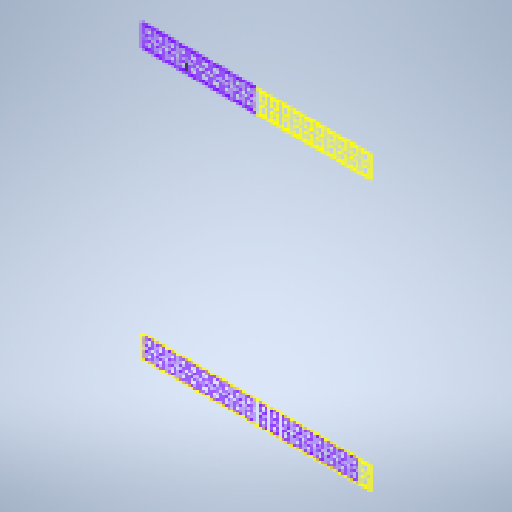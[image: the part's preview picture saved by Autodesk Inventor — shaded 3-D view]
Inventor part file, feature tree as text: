
AUTODESK INVENTOR PART (.ipt)
format: ipt  version: 2024.2 (Build 282272000, 272)  size: 213,504 bytes
history: native  units: in
note: dims shown in document units (in); Inventor stores cm internally (conversion verified against a paired STEP export)
features: other x3, sketch x1, reference x1
ambient origin geometry x8: Origin, YZ Plane, XZ Plane, XY Plane, X Axis, Y Axis, Z Axis, Center Point
feature tree (5):
  sketch  "Sketch1"
  reference  "Reference3"
  other  "<userpath>\Desktop\meca_robotbebou\iks01A2\iks01A2switch.iam"
  other  "iks01A2switch.iam"
  other  "zl262-20d_p2-54_l25-9_w5_h8-5:3"
